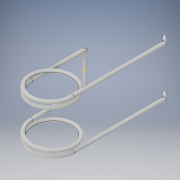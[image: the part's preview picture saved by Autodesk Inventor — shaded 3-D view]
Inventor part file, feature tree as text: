
AUTODESK INVENTOR PART (.ipt)
format: ipt  version: 2018 (Build 220112000, 112)  size: 257,024 bytes
history: native  units: in
note: dims shown in document units (in); Inventor stores cm internally (conversion verified against a paired STEP export)
features: sketch x9, extrude x6, projected_geometry x6, mirror x3, fillet x2, helix x1, plane x1, sweep x1
ambient origin geometry x8: Origin, YZ Plane, XZ Plane, XY Plane, X Axis, Y Axis, Z Axis, Center Point
bodies: Solid1 (feature_tree)
feature tree (29):
  helix  "Coil1"  [1 undecoded]
  extrude  "Extrusion1"  Depth=0.95in TaperAngle=0.0deg
  extrude  "Extrusion2"  Depth=0.0175in
  extrude  "Extrusion3"  Depth=0.035in
  extrude  "Extrusion4"  Depth=0.1925in TaperAngle=0.0deg
  extrude  "Extrusion5"  Depth=0.1in
  plane  "Work Plane1"
  mirror  "Mirror1"
  sweep  "Sweep1"
  fillet  "Fillet1"  Radius=0.035in
  extrude  "Extrusion6"  Depth=0.1925in TaperAngle=0.0deg
  mirror  "Mirror2"
  fillet  "Fillet2"  Radius=0.035in
  mirror  "Mirror3"
  sketch  "Sketch1"  dims[d1=0.215in]
  sketch  "Sketch2"  dims[d2=0.075in d3=0.075in d4=0.5906in d5=0.0in d6=90.0deg d7=90.0deg d8=0.0in d9=0.0in d10=0.95in d11=0.0in]
  projected_geometry  "Projected Loop1"
  sketch  "Sketch3"  dims[d12=0.575in d13=0.0in d14=0.0175in]
  sketch  "Sketch4"  dims[d15=0.175in d16=0.0in d17=0.035in]
  projected_geometry  "Projected Loop2"
  sketch  "Sketch5"  dims[d18=0.1925in d19=0.0in d20=0.1925in d21=0.0in]
  projected_geometry  "Projected Loop3"
  sketch  "Sketch6"  dims[d22=0.0in d23=0.1in]
  projected_geometry  "Projected Loop4"
  sketch  "Sketch7"  dims[d24=45.0deg d25=0.0in d26=0.0in d27=0.035in]
  projected_geometry  "Projected Loop5"
  sketch  "Sketch8"  dims[d28=45.0deg d29=0.1925in d30=0.0in d31=0.035in]
  projected_geometry  "Projected Loop6"
  sketch  "Sketch9"
note: 1 required parameter value undecoded (feature->parameter linkage not recoverable at this tier; creation-order binding heuristic only, values carry confidence <= 0.55)
